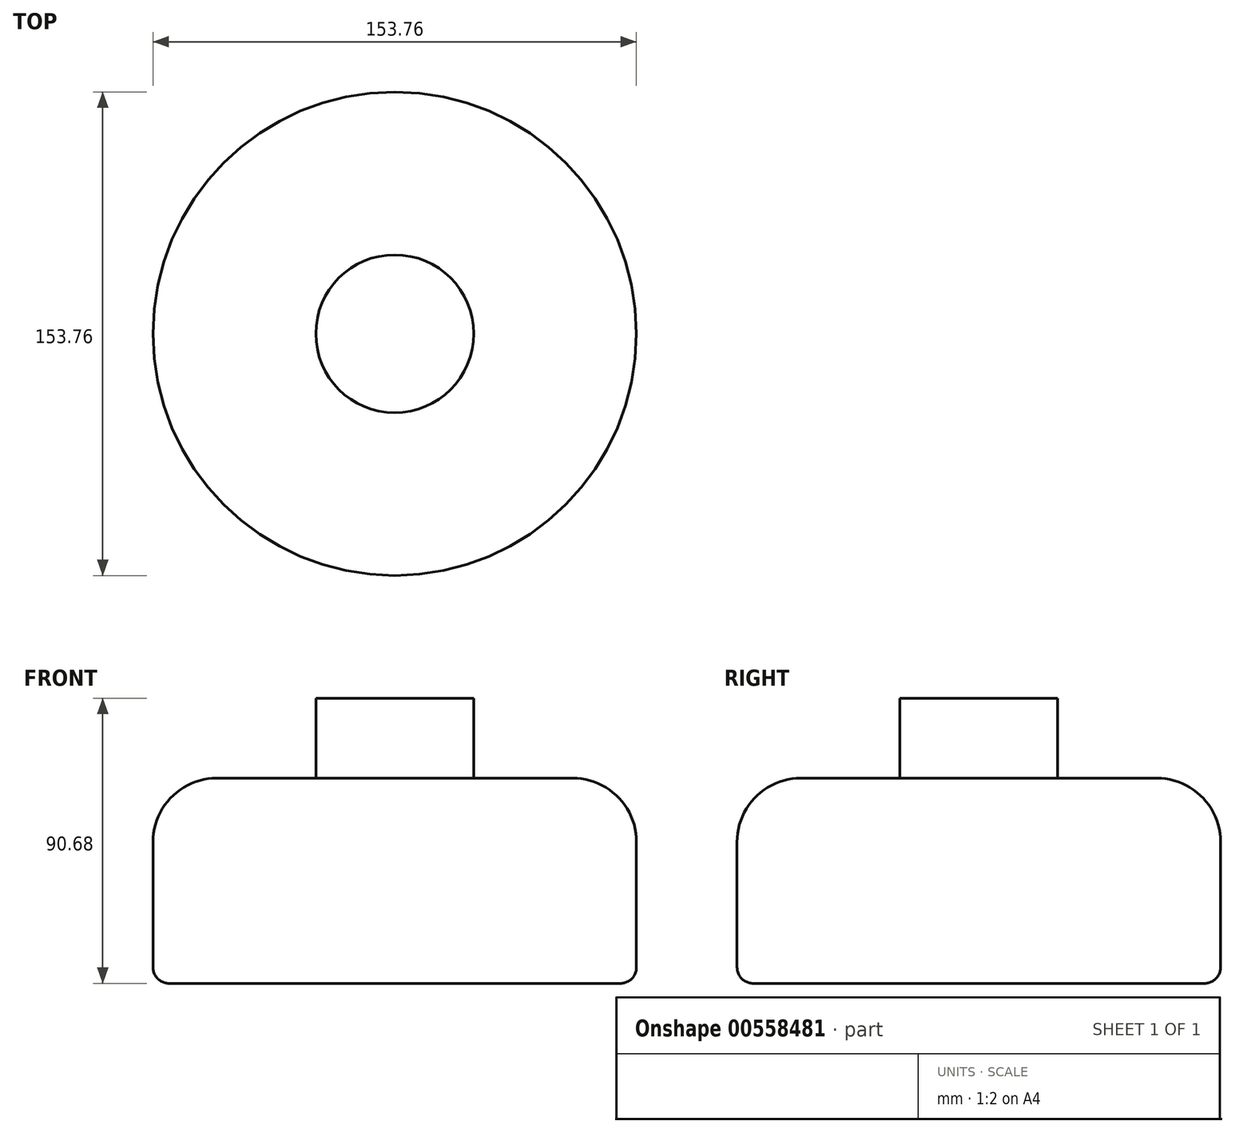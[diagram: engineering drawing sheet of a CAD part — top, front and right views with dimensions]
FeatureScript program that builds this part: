
annotation { "Feature Type Name" : "Feature", "Feature Type Description" : "" }
export const myFeature = defineFeature(function(context is Context, id is Id, definition is map)
    precondition{}
    {
        {
            var Q0;
            Q0=qCreatedBy(makeId("Top.planeOp"),FACE);
            var sketch = newSketch(context, id + "F0", { "sketchPlane" : qUnion([Q0])});
            skCircle(sketch, "E0", {"center": v(0, 0) * mm, "radius": 76.88 * mm});
            skSolve(sketch);
        }
        {
            var Q0;
            Q0 = qSketchRegion(id + "F0", true);
            extrude(context, id + "F1", {"entities" : qUnion([Q0]), "depth" : 65.28 * mm, "offsetDistance" : 25.4 * mm});
        }
        {
            var Q0;
            Q0=makeQuery(id+"F1.opExtrude","CAP_FACE",FACE,{"disambiguationData":[OSD([sQuery(id+"F0.wireOp",EDGE,"E0")])],"isStart":false});
            var sketch = newSketch(context, id + "F2", { "sketchPlane" : qUnion([Q0])});
            skCircle(sketch, "E1", {"center": v(0, 0) * mm, "radius": 25.08 * mm});
            skSolve(sketch);
        }
        {
            var Q0;
            Q0 = qSketchRegion(id + "F2", true);
            extrude(context, id + "F3", {"entities" : qUnion([Q0]), "operationType" : NewBodyOperationType.ADD, "depth" : 25.4 * mm, "offsetDistance" : 25.4 * mm});
        }
        {
            var Q0;
            Q0=makeQuery(id+"F1.opExtrude","CAP_EDGE",EDGE,{"disambiguationData":[OSD([sQuery(id+"F0.wireOp",EDGE,"E0")])],"isStart":true});
            fillet(context, id + "F4", {"entities" : qUnion([Q0]), "radius" : 5.08 * mm, "tangentPropagation" : true, "allowEdgeOverflow" : false});
        }
        {
            var Q0;
            Q0=makeQuery(id+"F1.opExtrude","CAP_EDGE",EDGE,{"disambiguationData":[OSD([sQuery(id+"F0.wireOp",EDGE,"E0")])],"isStart":false});
            fillet(context, id + "F5", {"entities" : qUnion([Q0]), "radius" : 20.32 * mm, "tangentPropagation" : true, "allowEdgeOverflow" : false});
        }
    });
